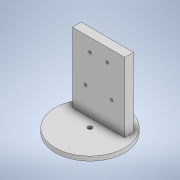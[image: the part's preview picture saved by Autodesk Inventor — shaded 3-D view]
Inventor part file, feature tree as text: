
AUTODESK INVENTOR PART (.ipt)
format: ipt  version: 2022 (Build 260153000, 153)  size: 127,488 bytes
history: native  units: mm
features: extrude x3, sketch x3
ambient origin geometry x8: Origin, YZ Plane, XZ Plane, XY Plane, X Axis, Y Axis, Z Axis, Center Point
bodies: Solid1 (feature_tree)
feature tree (6):
  extrude  "Extrusion1"  Depth=5.0mm
  extrude  "Extrusion2"  Depth=5.0mm
  extrude  "Extrusion3"  Depth=80.0mm TaperAngle=0.0deg
  sketch  "Sketch1"  dims[d0=80.0mm d1=5.0mm]
  sketch  "Sketch2"  dims[d2=5.0mm d3=0.0mm d5=30.0mm]
  sketch  "Sketch3"  dims[d6=10.0mm d8=80.0mm d9=0.0mm d13=3.0mm d14=3.0mm d18=3.0mm d19=3.0mm d20=5.0mm d21=0.0mm]
